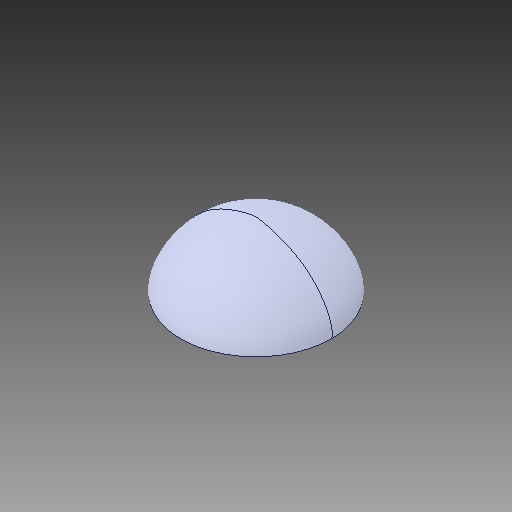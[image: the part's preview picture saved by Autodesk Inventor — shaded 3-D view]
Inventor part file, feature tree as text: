
AUTODESK INVENTOR PART (.ipt)
format: ipt  version: 2018.2 (Build 222227000, 227)  size: 123,392 bytes
history: native  units: mm
features: revolve x1
ambient origin geometry x8: Origin, YZ Plane, XZ Plane, XY Plane, X Axis, Y Axis, Z Axis, Center Point
bodies: Solido1 (feature_tree)
feature tree (1):
  revolve  "Revolve1"  [1 undecoded]
note: 1 required parameter value undecoded (feature->parameter linkage not recoverable at this tier; creation-order binding heuristic only, values carry confidence <= 0.55)
